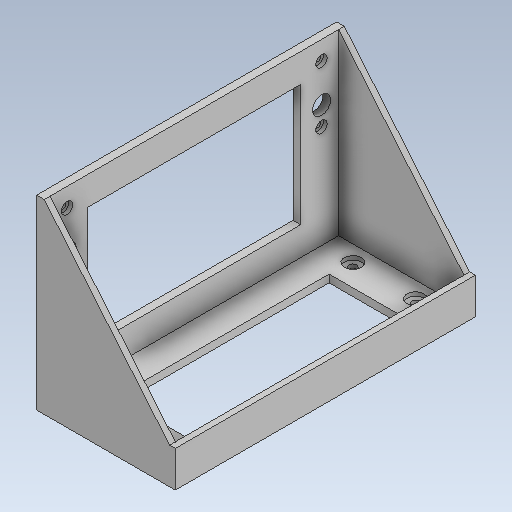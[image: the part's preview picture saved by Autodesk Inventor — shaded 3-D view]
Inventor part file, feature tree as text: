
AUTODESK INVENTOR PART (.ipt)
format: ipt  version: 2021 (Build 250183000, 183)  size: 266,752 bytes
history: native  units: mm
features: extrude x13, sketch x11, reference x4, other x4
ambient origin geometry x8: Origin, YZ Plane, XZ Plane, XY Plane, X Axis, Y Axis, Z Axis, Center Point
bodies: Solid1 (feature_tree)
feature tree (32):
  sketch  "Sketch1"  dims[d0=152.0mm d1=66.0mm]
  extrude  "Extrusion1"  Depth=66.0mm
  extrude  "Extrusion2"  Depth=3.0mm
  sketch  "Sketch7"  dims[d2=3.0mm d3=3.0mm]
  extrude  "Extrusion3"  Depth=4.0mm TaperAngle=0.0deg
  extrude  "Extrusion4"  Depth=3.0mm
  extrude  "Extrusion5"  Depth=15.0mm TaperAngle=0.0deg
  extrude  "Extrusion6"  Depth=3.0mm TaperAngle=0.0deg
  extrude  "Extrusion7"  Depth=15.0mm
  extrude  "Extrusion8"  Depth=15.0mm
  extrude  "Extrusion9"  Depth=20.0mm
  extrude  "Extrusion10"  Depth=3.0mm TaperAngle=0.0deg
  extrude  "Extrusion11"  Depth=15.0mm
  extrude  "Extrusion12"  Depth=20.0mm
  extrude  "Extrusion13"  Depth=15.0mm
  sketch  "Sketch8"  dims[d4=4.0mm d5=4.0mm d6=0.0mm]
  sketch  "Sketch9"  dims[d7=94.0mm d8=0.0mm d15=3.0mm]
  sketch  "Sketch10"  dims[d16=94.0mm d17=0.0mm d18=15.0mm d19=0.0mm]
  sketch  "Sketch11"  dims[d20=3.0mm d21=0.0mm d22=3.0mm d23=0.0mm]
  sketch  "Sketch12"  dims[d24=20.0mm d25=15.0mm]
  sketch  "Sketch13"  dims[d26=20.0mm d27=15.0mm]
  reference  "Reference1"
  reference  "Reference2"
  reference  "Reference3"
  reference  "Reference4"
  sketch  "Sketch14"  dims[d28=20.0mm d29=20.0mm]
  sketch  "Sketch15"  dims[d30=15.0mm d31=3.0mm d32=0.0mm]
  sketch  "Sketch16"  dims[d33=20.0mm d34=15.0mm d35=20.0mm d36=15.0mm d37=20.0mm d38=15.0mm d39=20.0mm d40=15.0mm d41=3.0mm d42=0.0mm d43=23.0mm d44=11.5mm d45=20.0mm d46=20.0mm d47=4.0mm d48=4.0mm d49=11.5mm d50=20.0mm d51=20.0mm d52=4.0mm d53=4.0mm d54=3.0mm d55=0.0mm d56=3.0mm d57=0.0mm d58=20.103mm d59=9.534mm d60=3.0mm d61=0.0mm d68=9.0mm d69=9.0mm d70=9.0mm d71=9.0mm d72=2.0mm d73=0.0mm d74=6.0mm d75=6.0mm d76=6.0mm d77=6.0mm d78=2.0mm d79=0.0mm]
  parser-record x1  (decoder bookkeeping rows leaked as tree rows — omitted from the tree; the rows remain in map.json)
  other  "assembly.iam"
  other  "DIN_mount:17"
  other  "DIN_mount:16"
note: 1 file-system path scrubbed to <path> (originals preserved in map.json)
